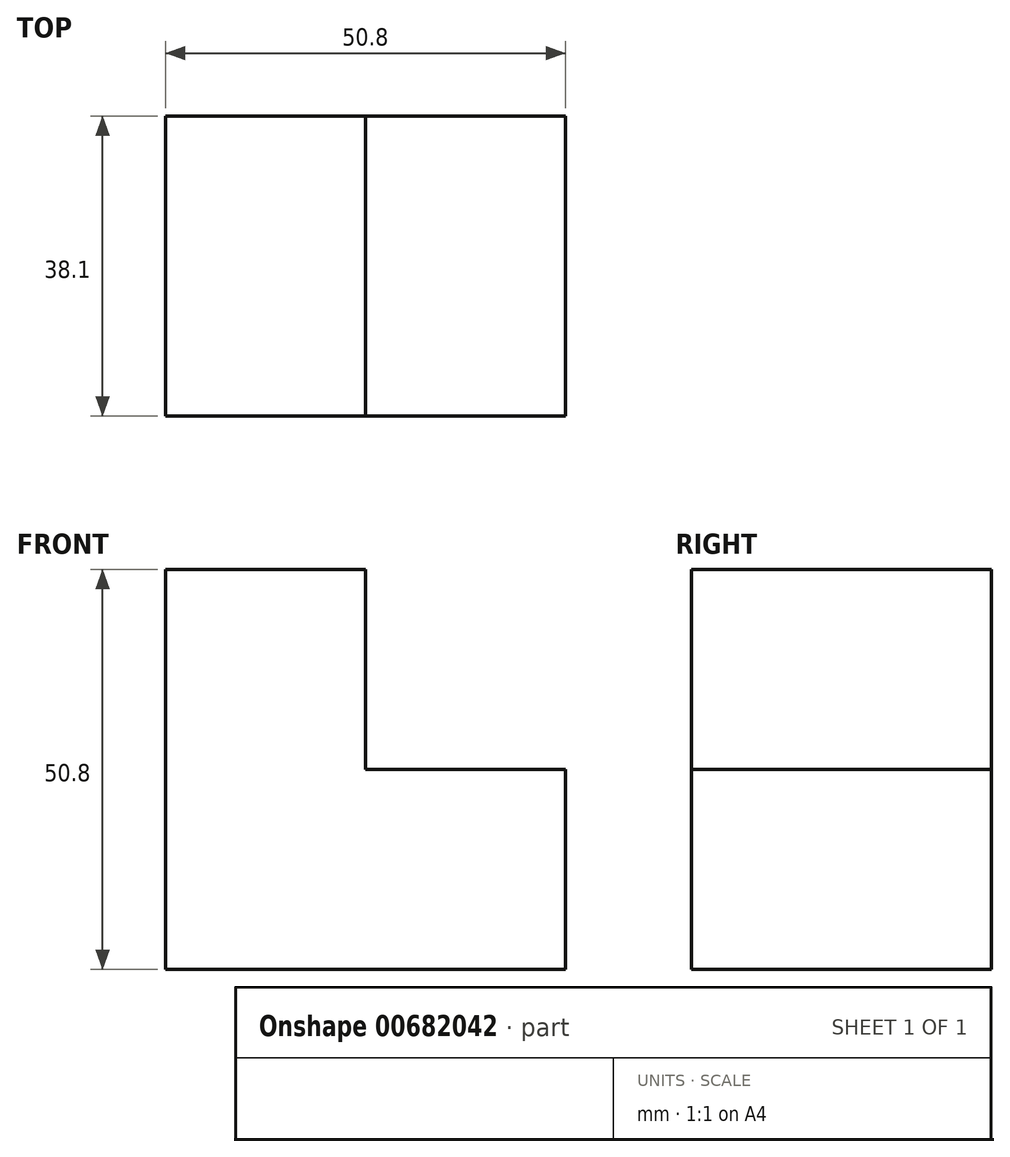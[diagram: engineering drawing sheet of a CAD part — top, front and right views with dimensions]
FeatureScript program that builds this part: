
annotation { "Feature Type Name" : "Feature", "Feature Type Description" : "" }
export const myFeature = defineFeature(function(context is Context, id is Id, definition is map)
    precondition{}
    {
        {
            var Q0;
            Q0=qCreatedBy(makeId("Front.planeOp"),FACE);
            var sketch = newSketch(context, id + "F0", { "sketchPlane" : qUnion([Q0])});
            skLineSegment(sketch, "E0", {"start": v(-42.6, 25.4) * mm, "end": v(-42.6, -25.4) * mm});
            skLineSegment(sketch, "E1", {"start": v(-42.6, -25.4) * mm, "end": v(8.2, -25.4) * mm});
            skLineSegment(sketch, "E2", {"start": v(8.2, -25.4) * mm, "end": v(8.2, 0) * mm});
            skLineSegment(sketch, "E3", {"start": v(8.2, 0) * mm, "end": v(-17.2, 0) * mm});
            skLineSegment(sketch, "E4", {"start": v(-17.2, 0) * mm, "end": v(-17.2, 25.4) * mm});
            skLineSegment(sketch, "E5", {"start": v(-17.2, 25.4) * mm, "end": v(-42.6, 25.4) * mm});
            skSolve(sketch);
        }
        {
            var Q0;
            Q0 = qSketchRegion(id + "F0", true);
            extrude(context, id + "F1", {"entities" : qUnion([Q0]), "depth" : 38.1 * mm, "offsetDistance" : 25.4 * mm});
        }
    });
